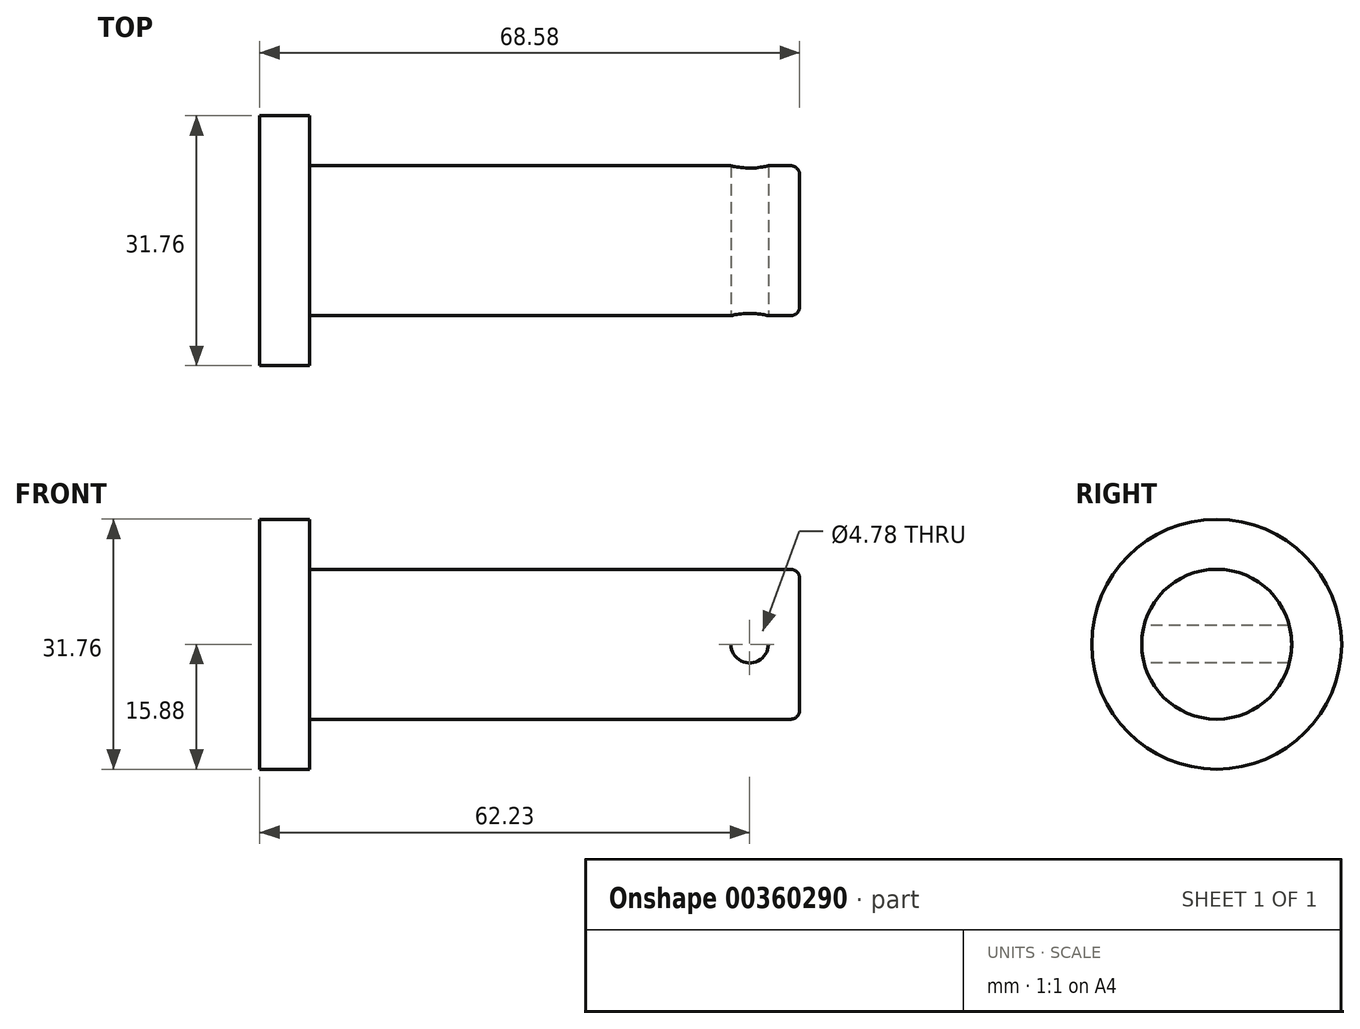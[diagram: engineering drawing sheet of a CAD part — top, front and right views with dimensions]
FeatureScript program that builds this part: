
annotation { "Feature Type Name" : "Feature", "Feature Type Description" : "" }
export const myFeature = defineFeature(function(context is Context, id is Id, definition is map)
    precondition{}
    {
        {
            var Q0;
            Q0=qCreatedBy(makeId("Right.planeOp"),FACE);
            var sketch = newSketch(context, id + "F0", { "sketchPlane" : qUnion([Q0])});
            skCircle(sketch, "E0", {"center": v(0, 0) * mm, "radius": 15.88 * mm});
            skSolve(sketch);
        }
        {
            var Q0;
            Q0 = qSketchRegion(id + "F0", true);
            extrude(context, id + "F1", {"entities" : qUnion([Q0]), "depth" : 6.35 * mm});
        }
        {
            var Q0;
            Q0=makeQuery(id+"F1.opExtrude","CAP_FACE",FACE,{"disambiguationData":[OSD([sQuery(id+"F0.wireOp",EDGE,"E0")])],"isStart":false});
            var sketch = newSketch(context, id + "F2", { "sketchPlane" : qUnion([Q0])});
            skLineSegment(sketch, "E1", {"start": v(0, 0) * mm, "end": v(9.53, 0) * mm});
            skLineSegment(sketch, "E2", {"start": v(9.53, 0) * mm, "end": v(0, 0) * mm});
            skLineSegment(sketch, "E3", {"start": v(0, 0) * mm, "end": v(-9.53, 0) * mm});
            skLineSegment(sketch, "E4", {"start": v(-9.53, 0) * mm, "end": v(0, 0) * mm});
            skLineSegment(sketch, "E5", {"start": v(0, 9.53) * mm, "end": v(0, 0) * mm});
            skLineSegment(sketch, "E6", {"start": v(0, 0) * mm, "end": v(0, -9.53) * mm});
            skLineSegment(sketch, "E7", {"start": v(0, -9.53) * mm, "end": v(-9.53, -9.53) * mm});
            skLineSegment(sketch, "E8", {"start": v(-9.53, -9.53) * mm, "end": v(-9.53, 0) * mm});
            skLineSegment(sketch, "E9", {"start": v(0, 9.53) * mm, "end": v(-9.53, 9.53) * mm});
            skLineSegment(sketch, "E10", {"start": v(-9.53, 9.53) * mm, "end": v(-9.53, 0) * mm});
            skLineSegment(sketch, "E11", {"start": v(9.53, 0) * mm, "end": v(9.53, 9.53) * mm});
            skLineSegment(sketch, "E12", {"start": v(9.53, 9.53) * mm, "end": v(0, 9.53) * mm});
            skLineSegment(sketch, "E13", {"start": v(9.53, 0) * mm, "end": v(9.53, -9.53) * mm});
            skLineSegment(sketch, "E14", {"start": v(9.53, -9.53) * mm, "end": v(0, -9.53) * mm});
            skSolve(sketch);
        }
        {
            var Q0;
            Q0 = qSketchRegion(id + "F2", true);
            extrude(context, id + "F3", {"entities" : qUnion([Q0]), "operationType" : NewBodyOperationType.ADD, "depth" : 62.23 * mm});
        }
        {
            var Q0;
            Q0=makeQuery(id+"F3.opExtrude","SWEPT_FACE",FACE,{"disambiguationData":[OSD([sQuery(id+"F2.wireOp",EDGE,"E8"),sQuery(id+"F2.wireOp",EDGE,"E10")])]});
            var sketch = newSketch(context, id + "F4", { "sketchPlane" : qUnion([Q0])});
            skLineSegment(sketch, "E15", {"start": v(68.58, 0) * mm, "end": v(62.23, 0) * mm});
            skCircle(sketch, "E16", {"center": v(62.23, 0) * mm, "radius": 2.39 * mm});
            skSolve(sketch);
        }
        {
            var Q0;
            Q0 = qSketchRegion(id + "F4", true);
            extrude(context, id + "F5", {"entities" : qUnion([Q0]), "operationType" : NewBodyOperationType.REMOVE, "oppositeDirection" : true, "depth" : 25.4 * mm});
        }
        {
            var Q0;
            Q0=makeQuery(id+"F3.opExtrude","SWEPT_EDGE",EDGE,{"disambiguationData":[OSD([sQuery(id+"F2.wireOp",EDGE,"E9"),sQuery(id+"F2.wireOp",EDGE,"E10")])]});
            var Q1;
            Q1=makeQuery(id+"F3.opExtrude","SWEPT_EDGE",EDGE,{"disambiguationData":[OSD([sQuery(id+"F2.wireOp",EDGE,"E11"),sQuery(id+"F2.wireOp",EDGE,"E12")])]});
            var Q2;
            Q2=makeQuery(id+"F3.opExtrude","SWEPT_EDGE",EDGE,{"disambiguationData":[OSD([sQuery(id+"F2.wireOp",EDGE,"E7"),sQuery(id+"F2.wireOp",EDGE,"E8")])]});
            var Q3;
            Q3=makeQuery(id+"F3.opExtrude","SWEPT_EDGE",EDGE,{"disambiguationData":[OSD([sQuery(id+"F2.wireOp",EDGE,"E13"),sQuery(id+"F2.wireOp",EDGE,"E14")])]});
            fillet(context, id + "F6", {"entities" : qUnion([Q0, Q1, Q2, Q3]), "radius" : 9.52 * mm, "tangentPropagation" : true, "allowEdgeOverflow" : false});
        }
        {
            var Q0;
            {var subQ0=sQuery(id+"F2.wireOp",EDGE,"E8");var subQ1=sQuery(id+"F2.wireOp",EDGE,"E7");Q0=makeQuery(id+"F6.opFillet","BLEND_EDGE",EDGE,{"blendedFrom":[makeQuery(id+"F3.opExtrude","SWEPT_EDGE",EDGE,{"disambiguationData":[OSD([subQ1,subQ0])]}),makeQuery(id+"F3.opExtrude","CAP_FACE",FACE,{"disambiguationData":[OSD([subQ1,subQ0,sQuery(id+"F2.wireOp",EDGE,"E9"),sQuery(id+"F2.wireOp",EDGE,"E10"),sQuery(id+"F2.wireOp",EDGE,"E11"),sQuery(id+"F2.wireOp",EDGE,"E12"),sQuery(id+"F2.wireOp",EDGE,"E13"),sQuery(id+"F2.wireOp",EDGE,"E14")])],"isStart":false})],"blendedInto":[makeQuery(id+"F3.opExtrude","CAP_FACE",FACE,{"disambiguationData":[OSD([subQ1,subQ0,sQuery(id+"F2.wireOp",EDGE,"E9"),sQuery(id+"F2.wireOp",EDGE,"E10"),sQuery(id+"F2.wireOp",EDGE,"E11"),sQuery(id+"F2.wireOp",EDGE,"E12"),sQuery(id+"F2.wireOp",EDGE,"E13"),sQuery(id+"F2.wireOp",EDGE,"E14")])],"isStart":false})]});}
            fillet(context, id + "F7", {"entities" : qUnion([Q0]), "radius" : 1.14 * mm, "tangentPropagation" : true, "allowEdgeOverflow" : false});
        }
    });
